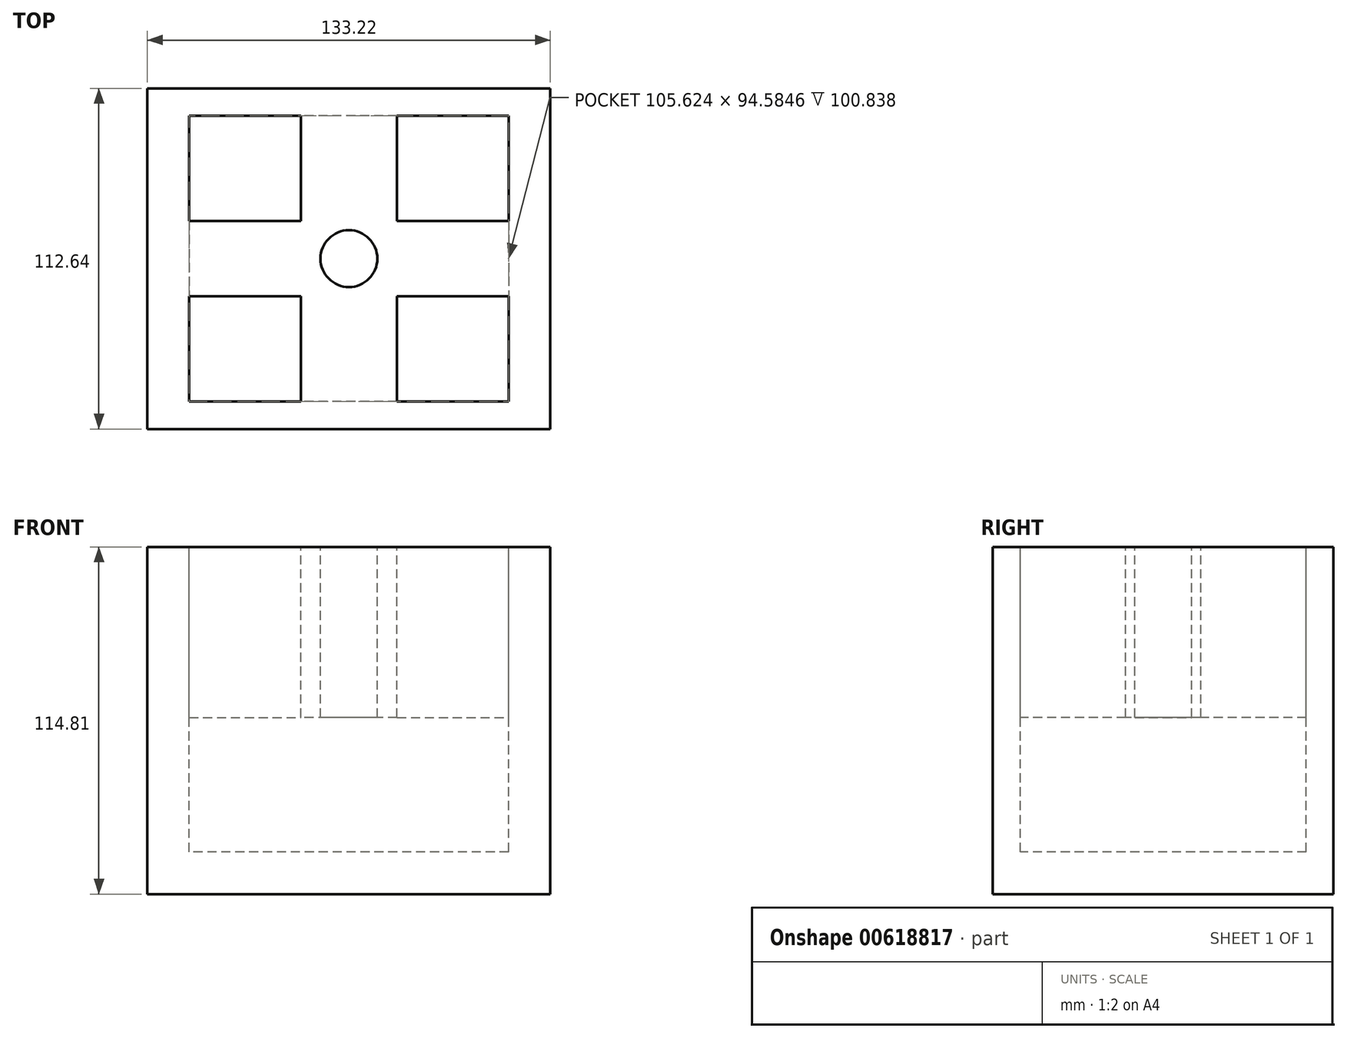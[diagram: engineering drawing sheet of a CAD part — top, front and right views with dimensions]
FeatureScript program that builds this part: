
annotation { "Feature Type Name" : "Feature", "Feature Type Description" : "" }
export const myFeature = defineFeature(function(context is Context, id is Id, definition is map)
    precondition{}
    {
        {
            var Q0;
            Q0=qCreatedBy(makeId("Top.planeOp"),FACE);
            var sketch = newSketch(context, id + "F0", { "sketchPlane" : qUnion([Q0])});
            skLineSegment(sketch, "E0.bottom", {"start": v(66.61, 56.32) * mm, "end": v(-66.61, 56.32) * mm});
            skLineSegment(sketch, "E0.top", {"start": v(66.61, -56.32) * mm, "end": v(-66.61, -56.32) * mm});
            skLineSegment(sketch, "E0.left", {"start": v(66.61, 56.32) * mm, "end": v(66.61, -56.32) * mm});
            skLineSegment(sketch, "E0.right", {"start": v(-66.61, 56.32) * mm, "end": v(-66.61, -56.32) * mm});
            skPoint(sketch, "E0.middle", {"position": v(0, 0) * mm});
            skSolve(sketch);
        }
        {
            var Q0;
            Q0=qSketchRegion(id+"F0",true);
            extrude(context, id + "F1", {"entities" : qUnion([Q0]), "depth" : 114.8 * mm, "offsetDistance" : 25.4 * mm});
        }
        {
            var Q0;
            Q0=makeQuery(id+"F1.opExtrude","CAP_FACE",FACE,{"disambiguationData":[OSD([sQuery(id+"F0.wireOp",EDGE,"E0.bottom"),sQuery(id+"F0.wireOp",EDGE,"E0.top"),sQuery(id+"F0.wireOp",EDGE,"E0.left"),sQuery(id+"F0.wireOp",EDGE,"E0.right")])],"isStart":false});
            var sketch = newSketch(context, id + "F2", { "sketchPlane" : qUnion([Q0])});
            skLineSegment(sketch, "E1.bottom", {"start": v(52.81, 47.3) * mm, "end": v(-52.81, 47.3) * mm});
            skLineSegment(sketch, "E1.top", {"start": v(52.81, -47.3) * mm, "end": v(-52.81, -47.3) * mm});
            skLineSegment(sketch, "E1.left", {"start": v(52.81, 47.3) * mm, "end": v(52.81, -47.3) * mm});
            skLineSegment(sketch, "E1.right", {"start": v(-52.81, 47.3) * mm, "end": v(-52.81, -47.3) * mm});
            skPoint(sketch, "E1.middle", {"position": v(0, 0) * mm});
            skSolve(sketch);
        }
        {
            var Q0;
            Q0=makeQuery(id+"F2.imprint","IMPRINT",FACE,{"disambiguationData":[TD([[makeQuery(id+"F2.imprint","IMPRINT",EDGE,{"derivedFrom":sQuery(id+"F2.wireOp",EDGE,"E1.bottom")}),1.0]])]});
            extrude(context, id + "F3", {"entities" : qUnion([Q0]), "operationType" : NewBodyOperationType.REMOVE, "oppositeDirection" : true, "depth" : 100.84 * mm, "offsetDistance" : 25.4 * mm});
        }
        {
            var Q0;
            Q0=makeQuery(id+"F1.opExtrude","CAP_FACE",FACE,{"disambiguationData":[OSD([sQuery(id+"F0.wireOp",EDGE,"E0.bottom"),sQuery(id+"F0.wireOp",EDGE,"E0.top"),sQuery(id+"F0.wireOp",EDGE,"E0.left"),sQuery(id+"F0.wireOp",EDGE,"E0.right")])],"isStart":false});
            var sketch = newSketch(context, id + "F4", { "sketchPlane" : qUnion([Q0])});
            skLineSegment(sketch, "E2.bottom", {"start": v(-15.93, 56.32) * mm, "end": v(15.93, 56.32) * mm});
            skLineSegment(sketch, "E2.top", {"start": v(-15.93, -56.32) * mm, "end": v(15.93, -56.32) * mm});
            skLineSegment(sketch, "E2.left", {"start": v(-15.93, 56.32) * mm, "end": v(-15.93, -56.32) * mm});
            skLineSegment(sketch, "E2.right", {"start": v(15.93, 56.32) * mm, "end": v(15.93, -56.32) * mm});
            skPoint(sketch, "E2.middle", {"position": v(0, 0) * mm});
            skLineSegment(sketch, "E3.bottom", {"start": v(-66.61, 12.42) * mm, "end": v(66.61, 12.42) * mm});
            skLineSegment(sketch, "E3.top", {"start": v(-66.61, -12.42) * mm, "end": v(66.61, -12.42) * mm});
            skLineSegment(sketch, "E3.left", {"start": v(-66.61, 12.42) * mm, "end": v(-66.61, -12.42) * mm});
            skLineSegment(sketch, "E3.right", {"start": v(66.61, 12.42) * mm, "end": v(66.61, -12.42) * mm});
            skSolve(sketch);
        }
        {
            var Q0;
            {var subQ0=sQuery(id+"F4.wireOp",EDGE,"E3.bottom");var subQ1=sQuery(id+"F4.wireOp",EDGE,"E2.left");var subQ2=makeQuery(id+"F4.imprint","INTERSECT",VERTEX,{"derivedFrom":[subQ1,subQ0]});Q0=makeQuery(id+"F4.imprint","IMPRINT",FACE,{"disambiguationData":[TD([[makeQuery(id+"F4.imprint","IMPRINT",EDGE,{"disambiguationData":[TD([[subQ2,-1.0]])],"derivedFrom":subQ1}),-1.0]])]});}
            var Q1;
            {var subQ0=sQuery(id+"F4.wireOp",EDGE,"E3.bottom");var subQ1=sQuery(id+"F4.wireOp",EDGE,"E2.right");var subQ2=makeQuery(id+"F4.imprint","INTERSECT",VERTEX,{"derivedFrom":[subQ1,subQ0]});Q1=makeQuery(id+"F4.imprint","IMPRINT",FACE,{"disambiguationData":[TD([[makeQuery(id+"F4.imprint","IMPRINT",EDGE,{"disambiguationData":[TD([[subQ2,-1.0]])],"derivedFrom":subQ1}),1.0]])]});}
            var Q2;
            {var subQ0=sQuery(id+"F4.wireOp",EDGE,"E3.bottom");var subQ1=sQuery(id+"F4.wireOp",EDGE,"E2.left");var subQ2=makeQuery(id+"F4.imprint","INTERSECT",VERTEX,{"derivedFrom":[subQ1,subQ0]});Q2=makeQuery(id+"F4.imprint","IMPRINT",FACE,{"disambiguationData":[TD([[makeQuery(id+"F4.imprint","IMPRINT",EDGE,{"disambiguationData":[TD([[subQ2,1.0]])],"derivedFrom":subQ1}),1.0]])]});}
            var Q3;
            {var subQ0=sQuery(id+"F4.wireOp",EDGE,"E3.top");var subQ1=sQuery(id+"F4.wireOp",EDGE,"E2.left");var subQ2=makeQuery(id+"F4.imprint","INTERSECT",VERTEX,{"derivedFrom":[subQ1,subQ0]});Q3=makeQuery(id+"F4.imprint","IMPRINT",FACE,{"disambiguationData":[TD([[makeQuery(id+"F4.imprint","IMPRINT",EDGE,{"disambiguationData":[TD([[subQ2,-1.0]])],"derivedFrom":subQ1}),1.0]])]});}
            var Q4;
            {var subQ0=sQuery(id+"F4.wireOp",EDGE,"E3.bottom");var subQ1=sQuery(id+"F4.wireOp",EDGE,"E2.left");var subQ2=makeQuery(id+"F4.imprint","INTERSECT",VERTEX,{"derivedFrom":[subQ1,subQ0]});Q4=makeQuery(id+"F4.imprint","IMPRINT",FACE,{"disambiguationData":[TD([[makeQuery(id+"F4.imprint","IMPRINT",EDGE,{"disambiguationData":[TD([[subQ2,-1.0]])],"derivedFrom":subQ1}),1.0]])]});}
            extrude(context, id + "F5", {"entities" : qUnion([Q0, Q1, Q2, Q3, Q4]), "operationType" : NewBodyOperationType.ADD, "oppositeDirection" : true, "depth" : 56.4 * mm, "offsetDistance" : 25.4 * mm});
        }
        {
            var Q0;
            Q0=makeQuery(id+"F5.boolean.opBoolean","MERGE",FACE,{"derivedFrom":[makeQuery(id+"F1.opExtrude","CAP_FACE",FACE,{"disambiguationData":[OSD([sQuery(id+"F0.wireOp",EDGE,"E0.bottom"),sQuery(id+"F0.wireOp",EDGE,"E0.top"),sQuery(id+"F0.wireOp",EDGE,"E0.left"),sQuery(id+"F0.wireOp",EDGE,"E0.right")])],"isStart":false}),makeQuery(id+"F5.opExtrude","CAP_FACE",FACE,{"disambiguationData":[OSD([sQuery(id+"F2.wireOp",EDGE,"E1.bottom"),sQuery(id+"F2.wireOp",EDGE,"E1.top"),sQuery(id+"F2.wireOp",EDGE,"E1.left"),sQuery(id+"F2.wireOp",EDGE,"E1.right"),sQuery(id+"F4.wireOp",EDGE,"E2.left"),sQuery(id+"F4.wireOp",EDGE,"E2.right"),sQuery(id+"F4.wireOp",EDGE,"E3.bottom"),sQuery(id+"F4.wireOp",EDGE,"E3.top")])],"isStart":true})]});
            var sketch = newSketch(context, id + "F6", { "sketchPlane" : qUnion([Q0])});
            skCircle(sketch, "E4", {"center": v(0, 0) * mm, "radius": 9.4 * mm});
            skSolve(sketch);
        }
        {
            var Q0;
            Q0=makeQuery(id+"F6.imprint","IMPRINT",FACE,{"disambiguationData":[TD([[makeQuery(id+"F6.imprint","IMPRINT",EDGE,{"derivedFrom":sQuery(id+"F6.wireOp",EDGE,"E4")}),1.0]])]});
            extrude(context, id + "F7", {"entities" : qUnion([Q0]), "operationType" : NewBodyOperationType.REMOVE, "oppositeDirection" : true, "depth" : 94.74 * mm, "offsetDistance" : 25.4 * mm});
        }
    });
